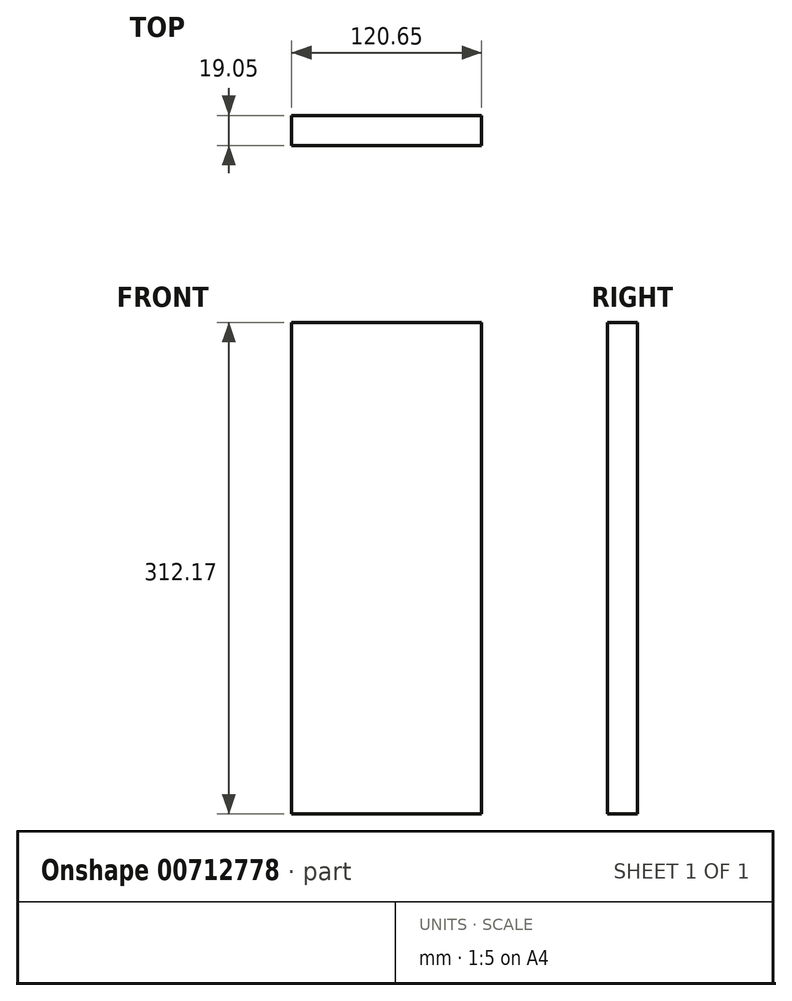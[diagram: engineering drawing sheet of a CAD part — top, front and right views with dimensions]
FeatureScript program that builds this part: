
annotation { "Feature Type Name" : "Feature", "Feature Type Description" : "" }
export const myFeature = defineFeature(function(context is Context, id is Id, definition is map)
    precondition{}
    {
        {
            var Q0;
            Q0=qCreatedBy(makeId("Front.planeOp"),FACE);
            var sketch = newSketch(context, id + "F0", { "sketchPlane" : qUnion([Q0])});
            skLineSegment(sketch, "E0.bottom", {"start": v(0, 0) * mm, "end": v(-120.65, 0) * mm});
            skLineSegment(sketch, "E0.top", {"start": v(0, 312.17) * mm, "end": v(-120.65, 312.17) * mm});
            skLineSegment(sketch, "E0.left", {"start": v(0, 0) * mm, "end": v(0, 312.17) * mm});
            skLineSegment(sketch, "E0.right", {"start": v(-120.65, 0) * mm, "end": v(-120.65, 312.17) * mm});
            skSolve(sketch);
        }
        {
            var Q0;
            Q0 = qSketchRegion(id + "F0", true);
            extrude(context, id + "F1", {"entities" : qUnion([Q0]), "depth" : 19.05 * mm, "offsetDistance" : 25.4 * mm});
        }
    });
